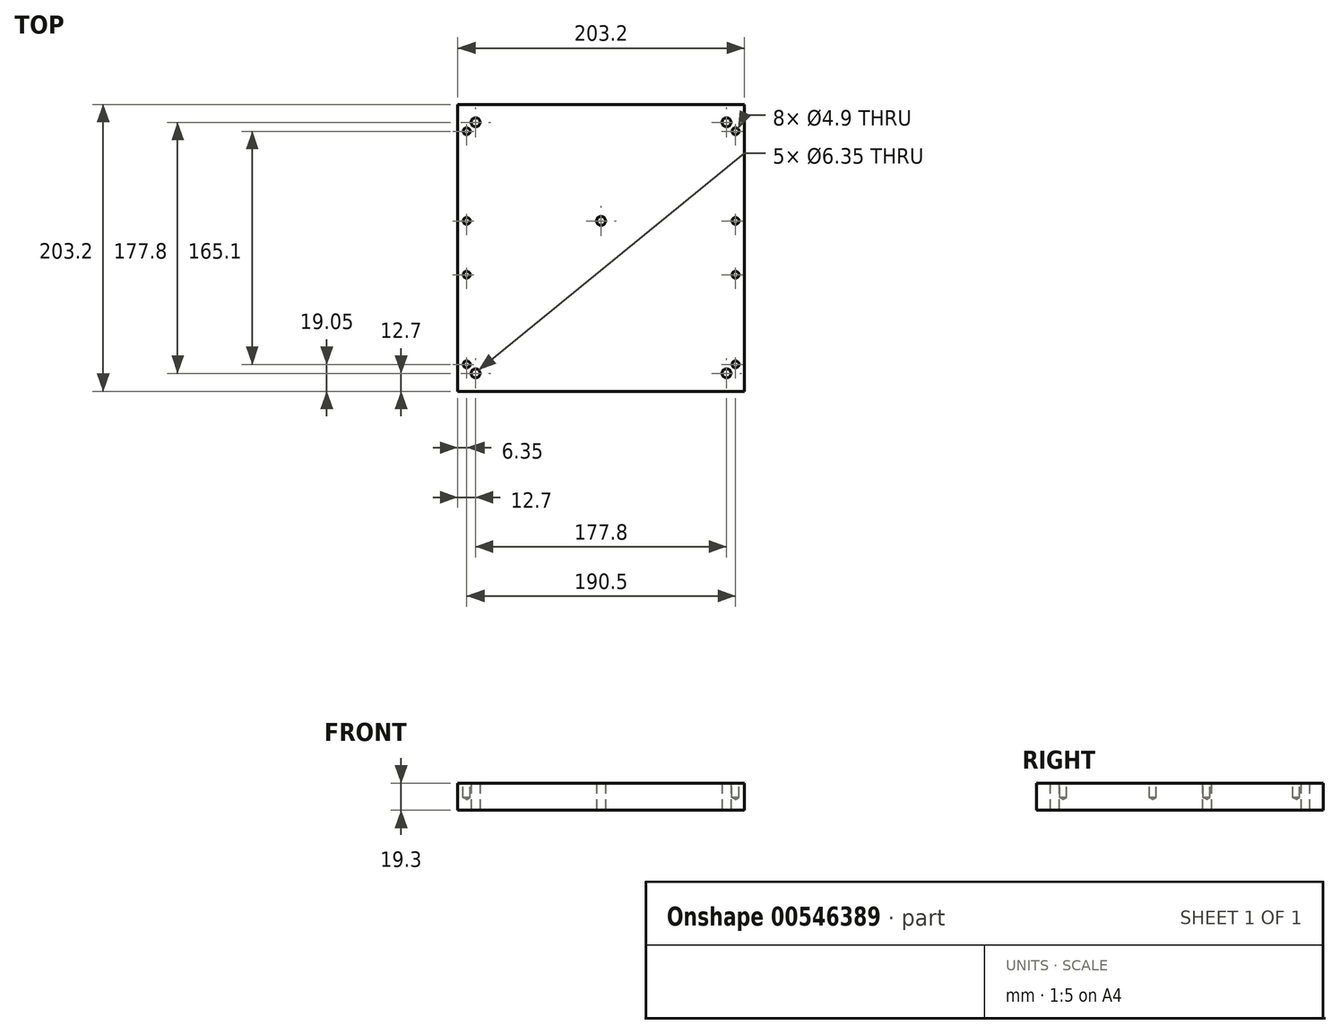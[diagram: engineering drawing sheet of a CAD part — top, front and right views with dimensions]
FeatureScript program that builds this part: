
annotation { "Feature Type Name" : "Feature", "Feature Type Description" : "" }
export const myFeature = defineFeature(function(context is Context, id is Id, definition is map)
    precondition{}
    {
        {
            var Q0;
            Q0=qCreatedBy(makeId("Top.planeOp"),FACE);
            var sketch = newSketch(context, id + "F0", { "sketchPlane" : qUnion([Q0])});
            skLineSegment(sketch, "E0.rect.bottom", {"start": v(101.6, -101.6) * mm, "end": v(-101.6, -101.6) * mm});
            skLineSegment(sketch, "E0.rect.top", {"start": v(101.6, 101.6) * mm, "end": v(-101.6, 101.6) * mm});
            skLineSegment(sketch, "E0.rect.left", {"start": v(101.6, -101.6) * mm, "end": v(101.6, 101.6) * mm});
            skLineSegment(sketch, "E0.rect.right", {"start": v(-101.6, -101.6) * mm, "end": v(-101.6, 101.6) * mm});
            skPoint(sketch, "E0.rect.middle", {"position": v(0, 0) * mm});
            skCircle(sketch, "E1", {"center": v(88.9, 88.9) * mm, "radius": 3.18 * mm});
            skCircle(sketch, "E2", {"center": v(-88.9, 88.9) * mm, "radius": 3.18 * mm});
            skCircle(sketch, "E3", {"center": v(-88.9, -88.9) * mm, "radius": 3.18 * mm});
            skCircle(sketch, "E4", {"center": v(88.9, -88.9) * mm, "radius": 3.18 * mm});
            skLineSegment(sketch, "E5.rect.bottom", {"start": v(88.9, 88.9) * mm, "end": v(-88.9, 88.9) * mm, "construction": true});
            skLineSegment(sketch, "E5.rect.top", {"start": v(88.9, -88.9) * mm, "end": v(-88.9, -88.9) * mm, "construction": true});
            skLineSegment(sketch, "E5.rect.left", {"start": v(88.9, 88.9) * mm, "end": v(88.9, -88.9) * mm, "construction": true});
            skLineSegment(sketch, "E5.rect.right", {"start": v(-88.9, 88.9) * mm, "end": v(-88.9, -88.9) * mm, "construction": true});
            skCircle(sketch, "E6", {"center": v(0, 19.05) * mm, "radius": 3.18 * mm});
            skPoint(sketch, "E7", {"position": v(-88.9, 0) * mm});
            skPoint(sketch, "E8", {"position": v(0, 88.9) * mm});
            skPoint(sketch, "E9", {"position": v(88.9, 0) * mm});
            skPoint(sketch, "E10", {"position": v(0, -88.9) * mm});
            skSolve(sketch);
        }
        {
            var Q0;
            Q0=qSketchRegion(id+"F0",true);
            extrude(context, id + "F1", {"entities" : qUnion([Q0]), "depth" : 19.3 * mm, "offsetDistance" : 25.4 * mm});
        }
        {
            var Q0;
            Q0=makeQuery(id+"F1.opExtrude","CAP_FACE",FACE,{"disambiguationData":[OSD([sQuery(id+"F0.wireOp",EDGE,"E0.rect.bottom"),sQuery(id+"F0.wireOp",EDGE,"E0.rect.top"),sQuery(id+"F0.wireOp",EDGE,"E0.rect.left"),sQuery(id+"F0.wireOp",EDGE,"E0.rect.right"),sQuery(id+"F0.wireOp",EDGE,"E1"),sQuery(id+"F0.wireOp",EDGE,"E2"),sQuery(id+"F0.wireOp",EDGE,"E3"),sQuery(id+"F0.wireOp",EDGE,"E4"),sQuery(id+"F0.wireOp",EDGE,"E6")])],"isStart":false});
            var sketch = newSketch(context, id + "F2", { "sketchPlane" : qUnion([Q0])});
            skLineSegment(sketch, "E11.0", {"start": v(-101.6, -101.6) * mm, "end": v(-101.6, 101.6) * mm});
            skLineSegment(sketch, "E11.1", {"start": v(101.6, 101.6) * mm, "end": v(-101.6, 101.6) * mm});
            skLineSegment(sketch, "E11.2", {"start": v(101.6, -101.6) * mm, "end": v(101.6, 101.6) * mm});
            skLineSegment(sketch, "E11.3", {"start": v(101.6, -101.6) * mm, "end": v(-101.6, -101.6) * mm});
            skLineSegment(sketch, "E12", {"start": v(-101.6, 0) * mm, "end": v(-95.25, 0) * mm});
            skLineSegment(sketch, "E13.0", {"start": v(-95.25, -95.25) * mm, "end": v(-95.25, 95.25) * mm});
            skLineSegment(sketch, "E13.1", {"start": v(95.25, -95.25) * mm, "end": v(-95.25, -95.25) * mm});
            skLineSegment(sketch, "E13.2", {"start": v(95.25, -95.25) * mm, "end": v(95.25, 95.25) * mm});
            skLineSegment(sketch, "E13.3", {"start": v(95.25, 95.25) * mm, "end": v(-95.25, 95.25) * mm});
            skLineSegment(sketch, "E14.0", {"start": v(88.9, -88.9) * mm, "end": v(-88.9, -88.9) * mm});
            skLineSegment(sketch, "E14.1", {"start": v(88.9, -88.9) * mm, "end": v(88.9, -6.35) * mm});
            skLineSegment(sketch, "E14.2", {"start": v(88.9, 88.9) * mm, "end": v(-88.9, 88.9) * mm});
            skLineSegment(sketch, "E14.3", {"start": v(-88.9, -88.9) * mm, "end": v(-88.9, -6.35) * mm});
            skLineSegment(sketch, "E15.trimOffspring", {"start": v(-88.9, -6.35) * mm, "end": v(88.9, -6.35) * mm});
            skLineSegment(sketch, "E16.trimOffspring", {"start": v(-88.9, 6.35) * mm, "end": v(-88.9, 88.9) * mm});
            skLineSegment(sketch, "E17.trimOffspring", {"start": v(-88.9, 0) * mm, "end": v(101.6, 0) * mm});
            skLineSegment(sketch, "E18.trimOffspring", {"start": v(-88.9, 6.35) * mm, "end": v(88.9, 6.35) * mm});
            skLineSegment(sketch, "E19.trimOffspring", {"start": v(88.9, 6.35) * mm, "end": v(88.9, 88.9) * mm});
            skLineSegment(sketch, "E20.bottom", {"start": v(-101.6, -101.6) * mm, "end": v(-82.55, -101.6) * mm});
            skLineSegment(sketch, "E20.top", {"start": v(-101.6, -82.55) * mm, "end": v(-82.55, -82.55) * mm});
            skLineSegment(sketch, "E20.left", {"start": v(-101.6, -101.6) * mm, "end": v(-101.6, -82.55) * mm});
            skLineSegment(sketch, "E20.right", {"start": v(-82.55, -101.6) * mm, "end": v(-82.55, -82.55) * mm});
            skLineSegment(sketch, "E21.bottom", {"start": v(-101.6, 101.6) * mm, "end": v(-82.55, 101.6) * mm});
            skLineSegment(sketch, "E21.top", {"start": v(-101.6, 82.55) * mm, "end": v(-82.55, 82.55) * mm});
            skLineSegment(sketch, "E21.left", {"start": v(-101.6, 101.6) * mm, "end": v(-101.6, 82.55) * mm});
            skLineSegment(sketch, "E21.right", {"start": v(-82.55, 101.6) * mm, "end": v(-82.55, 82.55) * mm});
            skLineSegment(sketch, "E22.bottom", {"start": v(101.6, 101.6) * mm, "end": v(82.55, 101.6) * mm});
            skLineSegment(sketch, "E22.top", {"start": v(101.6, 82.55) * mm, "end": v(82.55, 82.55) * mm});
            skLineSegment(sketch, "E22.left", {"start": v(101.6, 101.6) * mm, "end": v(101.6, 82.55) * mm});
            skLineSegment(sketch, "E22.right", {"start": v(82.55, 101.6) * mm, "end": v(82.55, 82.55) * mm});
            skLineSegment(sketch, "E23.bottom", {"start": v(101.6, 0) * mm, "end": v(82.55, 0) * mm});
            skLineSegment(sketch, "E23.top", {"start": v(101.6, 19.05) * mm, "end": v(82.55, 19.05) * mm});
            skLineSegment(sketch, "E23.left", {"start": v(101.6, 0) * mm, "end": v(101.6, 19.05) * mm});
            skLineSegment(sketch, "E23.right", {"start": v(82.55, 0) * mm, "end": v(82.55, 19.05) * mm});
            skLineSegment(sketch, "E24.top", {"start": v(101.6, -19.05) * mm, "end": v(82.55, -19.05) * mm});
            skLineSegment(sketch, "E24.left", {"start": v(101.6, 0) * mm, "end": v(101.6, -19.05) * mm});
            skLineSegment(sketch, "E24.right", {"start": v(82.55, 0) * mm, "end": v(82.55, -19.05) * mm});
            skLineSegment(sketch, "E25.bottom", {"start": v(101.6, -101.6) * mm, "end": v(82.55, -101.6) * mm});
            skLineSegment(sketch, "E25.top", {"start": v(101.6, -82.55) * mm, "end": v(82.55, -82.55) * mm});
            skLineSegment(sketch, "E25.left", {"start": v(101.6, -101.6) * mm, "end": v(101.6, -82.55) * mm});
            skLineSegment(sketch, "E25.right", {"start": v(82.55, -101.6) * mm, "end": v(82.55, -82.55) * mm});
            skLineSegment(sketch, "E26.bottom", {"start": v(-101.6, 0) * mm, "end": v(-82.55, 0) * mm});
            skLineSegment(sketch, "E26.top", {"start": v(-101.6, -19.05) * mm, "end": v(-82.55, -19.05) * mm});
            skLineSegment(sketch, "E26.left", {"start": v(-101.6, 0) * mm, "end": v(-101.6, -19.05) * mm});
            skLineSegment(sketch, "E26.right", {"start": v(-82.55, 0) * mm, "end": v(-82.55, -19.05) * mm});
            skLineSegment(sketch, "E27.top", {"start": v(-101.6, 19.05) * mm, "end": v(-82.55, 19.05) * mm});
            skLineSegment(sketch, "E27.left", {"start": v(-101.6, 0) * mm, "end": v(-101.6, 19.05) * mm});
            skLineSegment(sketch, "E27.right", {"start": v(-82.55, 0) * mm, "end": v(-82.55, 19.05) * mm});
            skPoint(sketch, "E28", {"position": v(-95.25, -82.55) * mm});
            skPoint(sketch, "E29", {"position": v(-95.25, -19.05) * mm});
            skPoint(sketch, "E30", {"position": v(-95.25, 19.05) * mm});
            skPoint(sketch, "E31", {"position": v(-95.25, 82.55) * mm});
            skPoint(sketch, "E32", {"position": v(-82.55, 95.25) * mm});
            skPoint(sketch, "E33", {"position": v(95.25, -82.55) * mm});
            skPoint(sketch, "E34", {"position": v(95.25, -19.05) * mm});
            skPoint(sketch, "E35", {"position": v(95.25, 19.05) * mm});
            skPoint(sketch, "E36", {"position": v(95.25, 82.55) * mm});
            skSolve(sketch);
        }
        {
            var Q0;
            Q0=sQuery(id+"F2.wireOp",VERTEX,"E28");
            var Q1;
            Q1=sQuery(id+"F2.wireOp",VERTEX,"E29");
            var Q2;
            Q2=sQuery(id+"F2.wireOp",VERTEX,"E30");
            var Q3;
            Q3=sQuery(id+"F2.wireOp",VERTEX,"E31");
            var Q4;
            Q4=sQuery(id+"F2.wireOp",VERTEX,"E36");
            var Q5;
            Q5=sQuery(id+"F2.wireOp",VERTEX,"E35");
            var Q6;
            Q6=sQuery(id+"F2.wireOp",VERTEX,"E34");
            var Q7;
            Q7=sQuery(id+"F2.wireOp",VERTEX,"E33");
            var Q8;
            Q8=makeQuery(id+"F1.opExtrude","SWEPT_BODY",BODY,{"disambiguationData":[OSD([sQuery(id+"F0.wireOp",EDGE,"E0.rect.bottom"),sQuery(id+"F0.wireOp",EDGE,"E0.rect.top"),sQuery(id+"F0.wireOp",EDGE,"E0.rect.left"),sQuery(id+"F0.wireOp",EDGE,"E0.rect.right"),sQuery(id+"F0.wireOp",EDGE,"E1"),sQuery(id+"F0.wireOp",EDGE,"E2"),sQuery(id+"F0.wireOp",EDGE,"E3"),sQuery(id+"F0.wireOp",EDGE,"E4"),sQuery(id+"F0.wireOp",EDGE,"E6")])]});
            hole(context, id + "F3", {"style" : HoleStyle.SIMPLE, "endStyle" : HoleEndStyle.BLIND, "holeDiameter" : 4.9 * mm, "holeDepth" : 10.16 * mm, "isTappedThrough" : true, "tappedDepth" : 12.7 * mm, "tapClearance" : 3, "locations" : qUnion([Q0, Q1, Q2, Q3, Q4, Q5, Q6, Q7]), "scope" : qUnion([Q8])});
        }
    });
